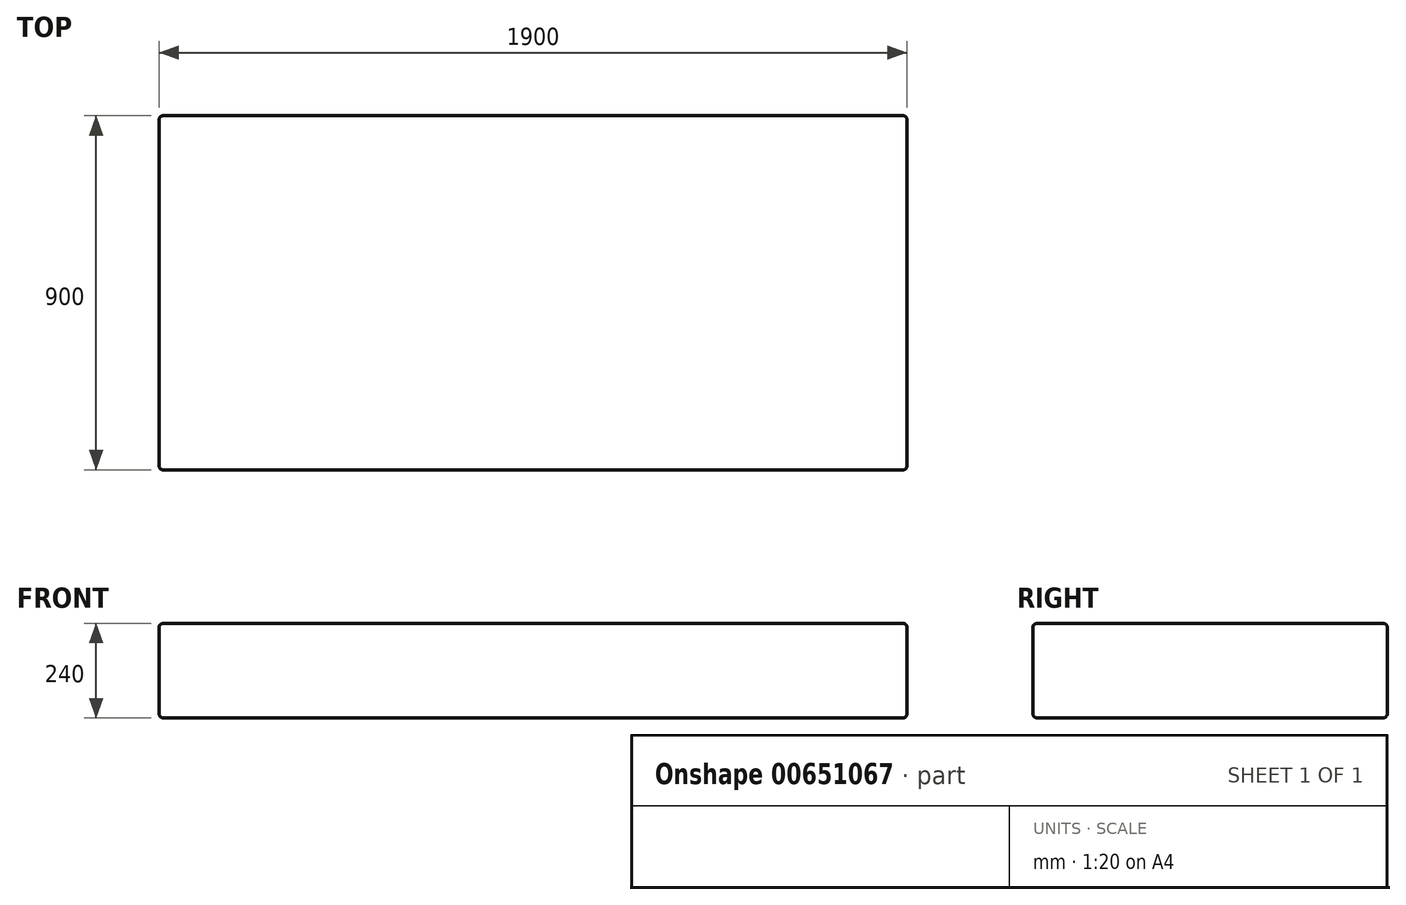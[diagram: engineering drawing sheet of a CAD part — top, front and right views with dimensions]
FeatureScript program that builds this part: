
annotation { "Feature Type Name" : "Feature", "Feature Type Description" : "" }
export const myFeature = defineFeature(function(context is Context, id is Id, definition is map)
    precondition{}
    {
        {
            var Q0;
            Q0=qCreatedBy(makeId("Top.planeOp"),FACE);
            var sketch = newSketch(context, id + "F0", { "sketchPlane" : qUnion([Q0])});
            skLineSegment(sketch, "E0.bottom", {"start": v(0, 0) * mm, "end": v(-1900, 0) * mm});
            skLineSegment(sketch, "E0.top", {"start": v(0, 900) * mm, "end": v(-1900, 900) * mm});
            skLineSegment(sketch, "E0.left", {"start": v(0, 0) * mm, "end": v(0, 900) * mm});
            skLineSegment(sketch, "E0.right", {"start": v(-1900, 0) * mm, "end": v(-1900, 900) * mm});
            skSolve(sketch);
        }
        {
            var Q0;
            Q0=qSketchRegion(id+"F0",true);
            extrude(context, id + "F1", {"entities" : qUnion([Q0]), "depth" : 240 * mm, "offsetDistance" : 25 * mm});
        }
        {
            var Q0;
            Q0=makeQuery(id+"F1.opExtrude","SWEPT_EDGE",EDGE,{"disambiguationData":[OSD([sQuery(id+"F0.wireOp",EDGE,"E0.top"),sQuery(id+"F0.wireOp",EDGE,"E0.left")])]});
            var Q1;
            Q1=makeQuery(id+"F1.opExtrude","SWEPT_EDGE",EDGE,{"disambiguationData":[OSD([sQuery(id+"F0.wireOp",EDGE,"E0.top"),sQuery(id+"F0.wireOp",EDGE,"E0.right")])]});
            var Q2;
            Q2=makeQuery(id+"F1.opExtrude","SWEPT_EDGE",EDGE,{"disambiguationData":[OSD([sQuery(id+"F0.wireOp",EDGE,"E0.bottom"),sQuery(id+"F0.wireOp",EDGE,"E0.left")])]});
            var Q3;
            Q3=makeQuery(id+"F1.opExtrude","SWEPT_EDGE",EDGE,{"disambiguationData":[OSD([sQuery(id+"F0.wireOp",EDGE,"E0.bottom"),sQuery(id+"F0.wireOp",EDGE,"E0.right")])]});
            var Q4;
            Q4=makeQuery(id+"F1.opExtrude","CAP_EDGE",EDGE,{"disambiguationData":[OSD([sQuery(id+"F0.wireOp",EDGE,"E0.bottom")])],"isStart":true});
            var Q5;
            Q5=makeQuery(id+"F1.opExtrude","CAP_EDGE",EDGE,{"disambiguationData":[OSD([sQuery(id+"F0.wireOp",EDGE,"E0.left")])],"isStart":true});
            var Q6;
            Q6=makeQuery(id+"F1.opExtrude","CAP_EDGE",EDGE,{"disambiguationData":[OSD([sQuery(id+"F0.wireOp",EDGE,"E0.top")])],"isStart":true});
            var Q7;
            Q7=makeQuery(id+"F1.opExtrude","CAP_EDGE",EDGE,{"disambiguationData":[OSD([sQuery(id+"F0.wireOp",EDGE,"E0.right")])],"isStart":true});
            var Q8;
            Q8=makeQuery(id+"F1.opExtrude","CAP_EDGE",EDGE,{"disambiguationData":[OSD([sQuery(id+"F0.wireOp",EDGE,"E0.bottom")])],"isStart":false});
            var Q9;
            Q9=makeQuery(id+"F1.opExtrude","CAP_EDGE",EDGE,{"disambiguationData":[OSD([sQuery(id+"F0.wireOp",EDGE,"E0.left")])],"isStart":false});
            var Q10;
            Q10=makeQuery(id+"F1.opExtrude","CAP_EDGE",EDGE,{"disambiguationData":[OSD([sQuery(id+"F0.wireOp",EDGE,"E0.top")])],"isStart":false});
            var Q11;
            Q11=makeQuery(id+"F1.opExtrude","CAP_EDGE",EDGE,{"disambiguationData":[OSD([sQuery(id+"F0.wireOp",EDGE,"E0.right")])],"isStart":false});
            fillet(context, id + "F2", {"entities" : qUnion([Q0, Q1, Q2, Q3, Q4, Q5, Q6, Q7, Q8, Q9, Q10, Q11]), "radius" : 10 * mm, "tangentPropagation" : true, "allowEdgeOverflow" : false});
        }
    });
